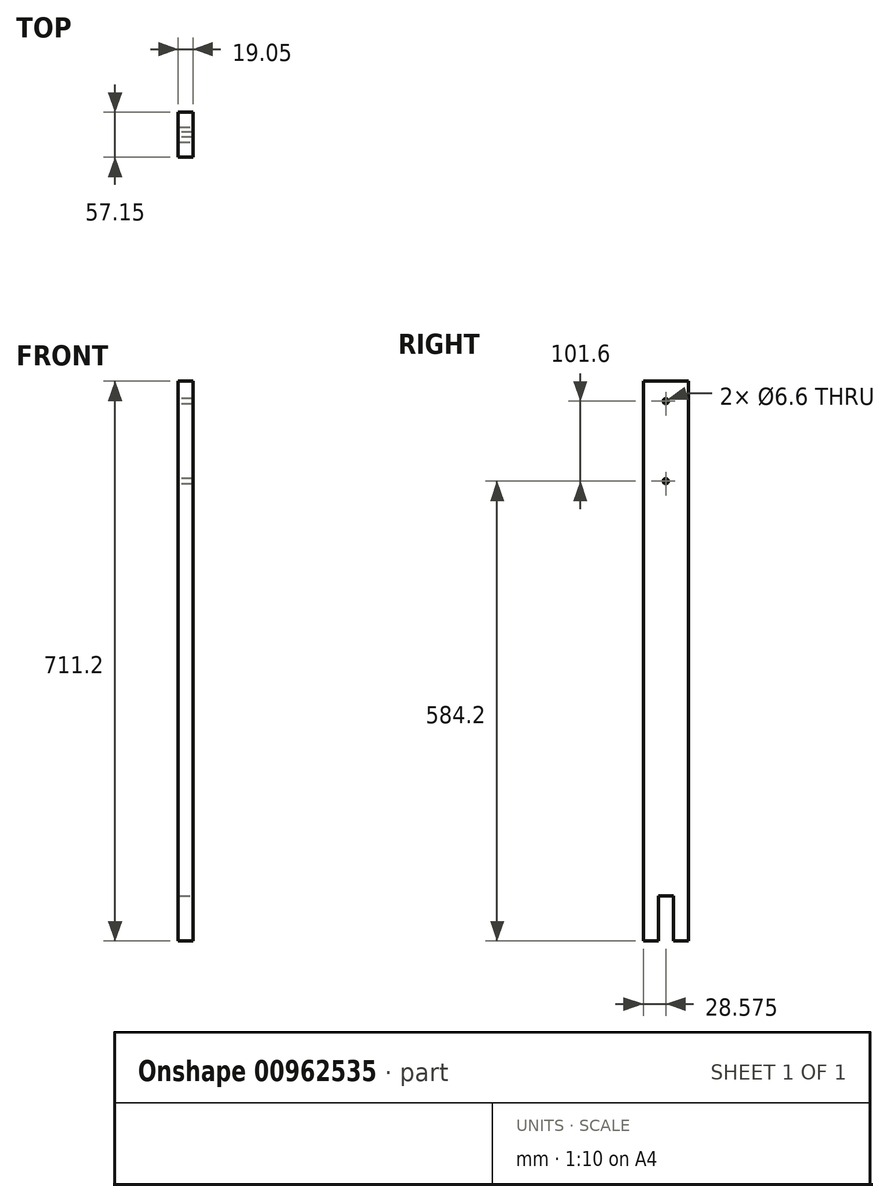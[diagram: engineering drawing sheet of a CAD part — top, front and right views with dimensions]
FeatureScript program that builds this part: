
annotation { "Feature Type Name" : "Feature", "Feature Type Description" : "" }
export const myFeature = defineFeature(function(context is Context, id is Id, definition is map)
    precondition{}
    {
        {
            var Q0;
            Q0=qCreatedBy(makeId("Top.planeOp"),FACE);
            var sketch = newSketch(context, id + "F0", { "sketchPlane" : qUnion([Q0])});
            skLineSegment(sketch, "E0.bottom", {"start": v(0, 0) * mm, "end": v(19.05, 0) * mm});
            skLineSegment(sketch, "E0.top", {"start": v(0, 57.15) * mm, "end": v(19.05, 57.15) * mm});
            skLineSegment(sketch, "E0.left", {"start": v(0, 0) * mm, "end": v(0, 57.15) * mm});
            skLineSegment(sketch, "E0.right", {"start": v(19.05, 0) * mm, "end": v(19.05, 57.15) * mm});
            skSolve(sketch);
        }
        {
            var Q0;
            Q0=makeQuery(id+"F0.imprint","IMPRINT",FACE,{"disambiguationData":[TD([[makeQuery(id+"F0.imprint","IMPRINT",EDGE,{"derivedFrom":sQuery(id+"F0.wireOp",EDGE,"E0.bottom")}),1.0]])]});
            extrude(context, id + "F1", {"entities" : qUnion([Q0]), "depth" : 711.2 * mm, "offsetDistance" : 25.4 * mm});
        }
        {
            var Q0;
            Q0=makeQuery(id+"F1.opExtrude","SWEPT_FACE",FACE,{"disambiguationData":[OSD([sQuery(id+"F0.wireOp",EDGE,"E0.right")])]});
            var sketch = newSketch(context, id + "F2", { "sketchPlane" : qUnion([Q0])});
            skLineSegment(sketch, "E1.bottom", {"start": v(19.05, 0) * mm, "end": v(38.1, 0) * mm});
            skLineSegment(sketch, "E1.top", {"start": v(19.05, 57.15) * mm, "end": v(38.1, 57.15) * mm});
            skLineSegment(sketch, "E1.left", {"start": v(19.05, 0) * mm, "end": v(19.05, 57.15) * mm});
            skLineSegment(sketch, "E1.right", {"start": v(38.1, 0) * mm, "end": v(38.1, 57.15) * mm});
            skSolve(sketch);
        }
        {
            var Q0;
            Q0=makeQuery(id+"F2.imprint","IMPRINT",FACE,{"disambiguationData":[TD([[makeQuery(id+"F2.imprint","IMPRINT",EDGE,{"derivedFrom":sQuery(id+"F2.wireOp",EDGE,"E1.bottom")}),1.0]])]});
            extrude(context, id + "F3", {"entities" : qUnion([Q0]), "operationType" : NewBodyOperationType.REMOVE, "endBound" : BoundingType.UP_TO_NEXT, "oppositeDirection" : true, "depth" : 25.4 * mm, "offsetDistance" : 25.4 * mm});
        }
        {
            var Q0;
            Q0=makeQuery(id+"F1.opExtrude","SWEPT_FACE",FACE,{"disambiguationData":[OSD([sQuery(id+"F0.wireOp",EDGE,"E0.left")])]});
            var sketch = newSketch(context, id + "F4", { "sketchPlane" : qUnion([Q0])});
            skLineSegment(sketch, "E2", {"start": v(-28.57, 711.2) * mm, "end": v(-28.57, 541.33) * mm, "construction": true});
            skCircle(sketch, "E3", {"center": v(-28.57, 685.8) * mm, "radius": 3.3 * mm});
            skCircle(sketch, "E4", {"center": v(-28.57, 584.2) * mm, "radius": 3.3 * mm});
            skSolve(sketch);
        }
        {
            var Q0;
            Q0 = qSketchRegion(id + "F4", true);
            extrude(context, id + "F5", {"entities" : qUnion([Q0]), "operationType" : NewBodyOperationType.REMOVE, "endBound" : BoundingType.UP_TO_NEXT, "oppositeDirection" : true, "depth" : 25.4 * mm, "offsetDistance" : 25.4 * mm});
        }
    });
